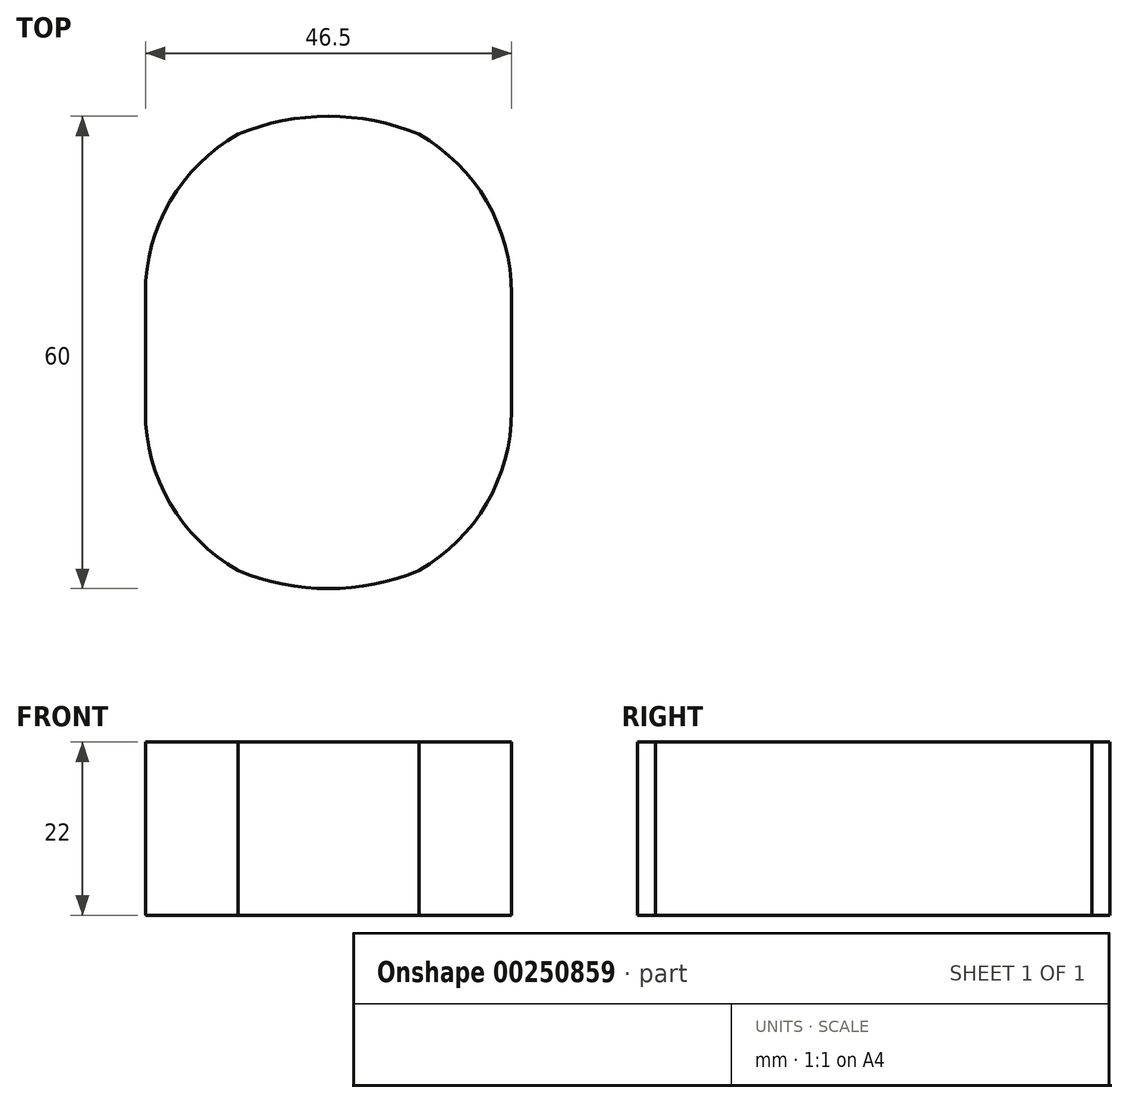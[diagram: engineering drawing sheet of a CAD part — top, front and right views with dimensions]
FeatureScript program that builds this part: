
annotation { "Feature Type Name" : "Feature", "Feature Type Description" : "" }
export const myFeature = defineFeature(function(context is Context, id is Id, definition is map)
    precondition{}
    {
        {
            var Q0;
            Q0=qCreatedBy(makeId("Top.planeOp"),FACE);
            var sketch = newSketch(context, id + "F0", { "sketchPlane" : qUnion([Q0])});
            skLineSegment(sketch, "E0.bottom", {"start": v(19, -7.5) * mm, "end": v(-19, -7.5) * mm});
            skLineSegment(sketch, "E0.top", {"start": v(19, 7.5) * mm, "end": v(-19, 7.5) * mm});
            skLineSegment(sketch, "E0.left", {"start": v(19, -7.5) * mm, "end": v(19, 7.5) * mm});
            skLineSegment(sketch, "E0.right", {"start": v(-19, -7.5) * mm, "end": v(-19, 7.5) * mm});
            skPoint(sketch, "E0.middle", {"position": v(0, 0) * mm});
            skSolve(sketch);
        }
        {
            var Q0;
            Q0=makeQuery(id+"F0.imprint","IMPRINT",FACE,{"disambiguationData":[TD([[makeQuery(id+"F0.imprint","IMPRINT",EDGE,{"derivedFrom":sQuery(id+"F0.wireOp",EDGE,"E0.bottom")}),-1.0]])]});
            var sketch = newSketch(context, id + "F1", { "sketchPlane" : qUnion([Q0])});
            skLineSegment(sketch, "E1.0", {"start": v(19, 7.5) * mm, "end": v(-19, 7.5) * mm, "construction": true});
            skLineSegment(sketch, "E2.0", {"start": v(10.26, 7.75) * mm, "end": v(-10.26, 7.75) * mm});
            skCircle(sketch, "E3", {"center": v(0, 17.75) * mm, "radius": 10 * mm});
            skSolve(sketch);
        }
        {
            var Q0;
            Q0=qCreatedBy(makeId("Top.planeOp"),FACE);
            var sketch = newSketch(context, id + "F2", { "sketchPlane" : qUnion([Q0])});
            skLineSegment(sketch, "E4", {"start": v(-29.23, 7.5) * mm, "end": v(31.33, 7.5) * mm, "construction": true});
            skCircle(sketch, "E5.0", {"center": v(0, 17.75) * mm, "radius": 10 * mm, "construction": true});
            skCircle(sketch, "E6.0", {"center": v(0, 17.75) * mm, "radius": 13 * mm, "construction": true});
            skArc(sketch, "E7", {"start": v(23.25, 7.5) * mm, "mid": v(0, 30.75) * mm, "end": v(-23.25, 7.5) * mm});
            skLineSegment(sketch, "E8", {"start": v(0, 30.75) * mm, "end": v(19.27, 30.75) * mm, "construction": true});
            skLineSegment(sketch, "E9", {"start": v(23.25, 7.5) * mm, "end": v(23.25, 0) * mm, "construction": true});
            skLineSegment(sketch, "E10", {"start": v(-23.25, 7.5) * mm, "end": v(-23.25, 0) * mm, "construction": true});
            skLineSegment(sketch, "E11", {"start": v(0, 0) * mm, "end": v(-23.25, 0) * mm, "construction": true});
            skLineSegment(sketch, "E12", {"start": v(23.25, 0) * mm, "end": v(0, 0) * mm, "construction": true});
            skArc(sketch, "E13.MirrorCS", {"start": v(23.25, -7.5) * mm, "mid": v(0, -30.75) * mm, "end": v(-23.25, -7.5) * mm});
            skLineSegment(sketch, "E14", {"start": v(-23.25, 7.5) * mm, "end": v(-23.25, -7.5) * mm});
            skLineSegment(sketch, "E15", {"start": v(23.25, 7.5) * mm, "end": v(23.25, -7.5) * mm});
            skSolve(sketch);
        }
        {
            var Q0;
            Q0 = qSketchRegion(id + "F2", true);
            extrude(context, id + "F3", {"entities" : qUnion([Q0]), "depth" : 22 * mm});
        }
        {
            var Q0;
            Q0=makeQuery(id+"F3.opExtrude","CAP_FACE",FACE,{"disambiguationData":[OSD([sQuery(id+"F2.wireOp",EDGE,"E7"),sQuery(id+"F2.wireOp",EDGE,"E13.MirrorCS"),sQuery(id+"F2.wireOp",EDGE,"E14"),sQuery(id+"F2.wireOp",EDGE,"E15")])],"isStart":false});
            var sketch = newSketch(context, id + "F4", { "sketchPlane" : qUnion([Q0])});
            skCircle(sketch, "E16", {"center": v(0, 0) * mm, "radius": 30 * mm});
            skSolve(sketch);
        }
        {
            var Q0;
            Q0 = qSketchRegion(id + "F4", true);
            extrude(context, id + "F5", {"entities" : qUnion([Q0]), "oppositeDirection" : true, "depth" : 25 * mm});
        }
        {
            var Q0;
            Q0=makeQuery(id+"F5.opExtrude","SWEPT_BODY",BODY,{"disambiguationData":[OSD([sQuery(id+"F4.wireOp",EDGE,"E16")])]});
            var Q1;
            Q1=makeQuery(id+"F3.opExtrude","SWEPT_BODY",BODY,{"disambiguationData":[OSD([sQuery(id+"F2.wireOp",EDGE,"E7"),sQuery(id+"F2.wireOp",EDGE,"E13.MirrorCS"),sQuery(id+"F2.wireOp",EDGE,"E14"),sQuery(id+"F2.wireOp",EDGE,"E15")])]});
            booleanBodies(context, id + "F6", {"operationType" : BooleanOperationType.INTERSECTION, "tools" : qUnion([Q0, Q1])});
        }
    });
